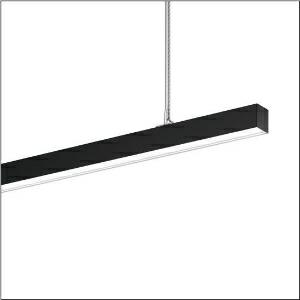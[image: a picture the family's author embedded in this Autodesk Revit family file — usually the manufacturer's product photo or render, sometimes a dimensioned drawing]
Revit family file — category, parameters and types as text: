
# Revit family: silica_r__21_51mx30tct9b_d278
name_source: partatom
category: Lighting Fixtures
units: mm (PartAtom-declared; Revit-internal decimal feet)

## family parameters
Cut with Voids When Loaded = No
Host = Face
Light Source = No
Part Type = Normal
Room Calculation Point = No
Round Connector Dimension = Use Diameter
Shared = No

## types (1)
- --- (1 x LED, 10300 lm, 84.4 W, 6500K)
    Apparent Load = 84 VA
    CIE Flux Codes = 47 79 96 58 100
    Color Rendering = 80
    Color Temperature = 6500K
    Default Elevation = 1800 mm
    Description = Silica® 21, office luminaire, primary optical cover: cover, of PMMA, opal, light emission: direct/indirect distribution, primary light characteristic: symmetric, installation type: suspended mounting, LED, rated luminous flux: 10.300lm, luminous efficacy: 116lm/W, light colour: 8tw, colour temperature: 2700..6500K, control gear: DALI DT8, with terminal, 3+2-pole, max. 2.5mm², mains connection: 220..240V, AC, 50/60Hz, rated input power: 88.7W, luminaire housing, of aluminium, matt jet black (RAL 9005), length: 3.004mm, width: 53mm, height: 53mm, protection rating (complete): IP20, insulation class (complete): insulation class I (protective earthing), certification: CE, permissible operating ambient temperature: 0..+35°C, standard: EN 50419, packaging unit: 1 piece
    Height = 53 mm
    Lamp = 1 x LED
    Lamp Light Flux = 10300 lm
    Lamp Power = 84.4 W
    Lamp count = 1
    Length = 3004 mm
    Luminous efficacy = 122 lm/W
    Manufacturer = Siteco
    ModVariant = No
    Model = 51MX30TCT9B
    Mounting Place = Ceiling
    Mounting Type = Pendant
    Number of Poles = 1
    OnlyDefault = Yes
    Power Factor = 1
    Product Name = Silica® 21
    Product group = office luminaire | ceiling pendant
    ProductGroupID = 903
    Protection Class = Protection class I
    Protection Degree = IP 20
    RLX_Detail_Level = 1
    RLX_Emergency_Light_Flux = 0 lm
    RLX_Emergency_Type = 0
    RLX_Emergency_Type_DB = No
    RlxData = <blob elided: 22769 chars, md5=4a6568e0>
    Socket = socket
    Standby Power = 0 W
    System Light Flux = 10300 lm
    System Power = 84 W
    Type Comments = individual setting
    Type Image = l_1335856.jpg
    URL = http://relux.com
    VarID = @adj_161105
    Voltage = 0 V
    Weight = 0.00 kg
    Width = 53 mm

## geometry (parser evidence)
native form markers: Blend x4, Sweep x15
no freeform markers — native parametric forms only
